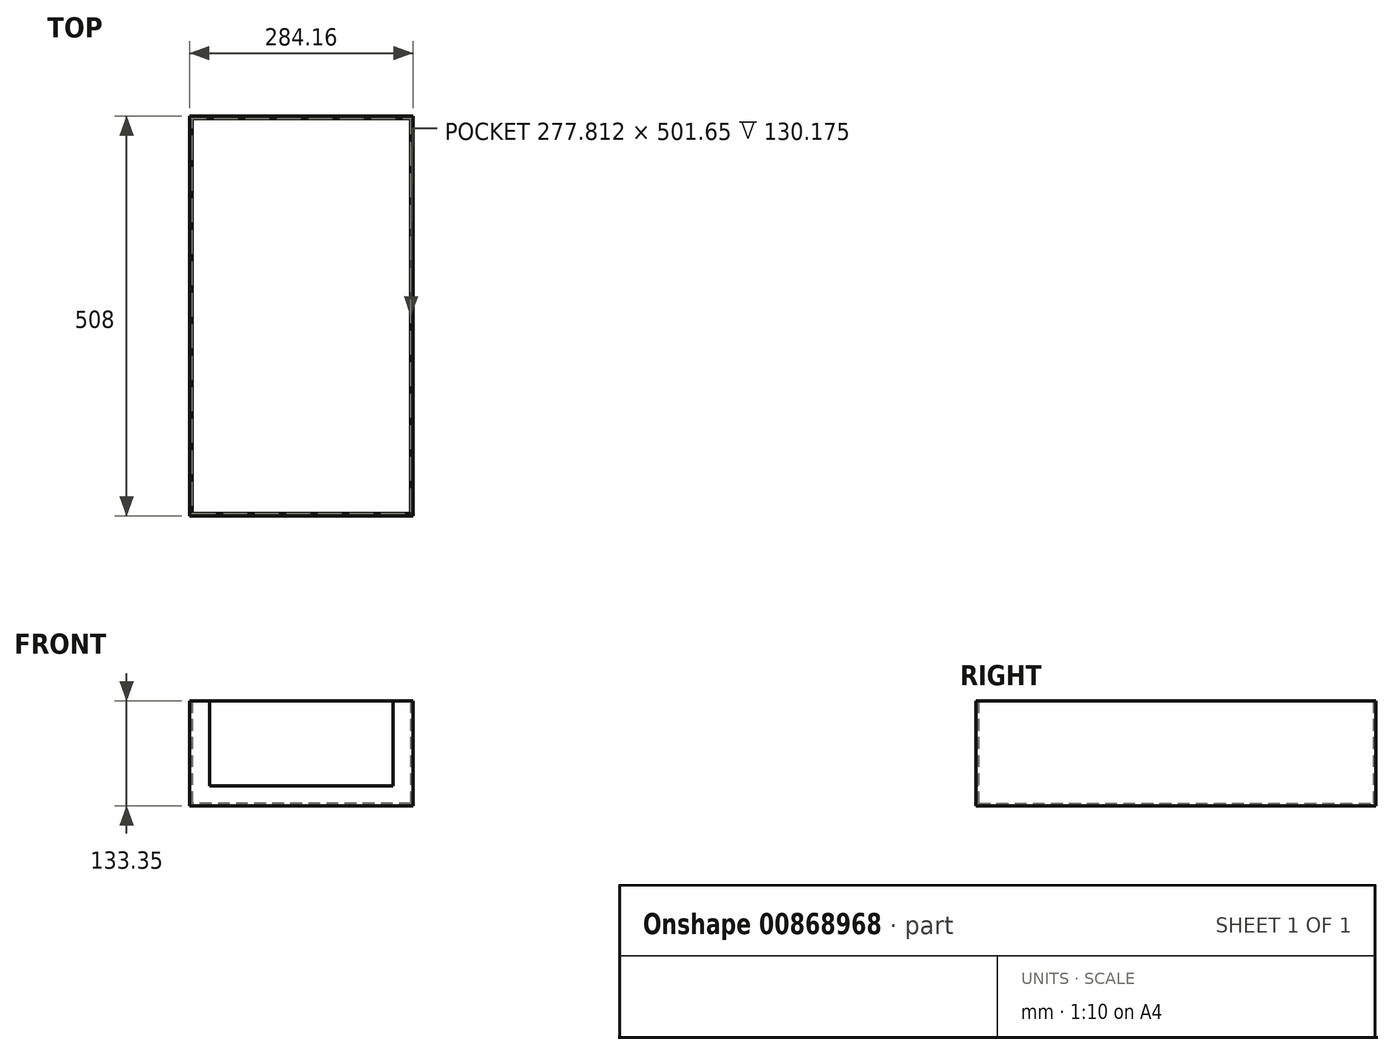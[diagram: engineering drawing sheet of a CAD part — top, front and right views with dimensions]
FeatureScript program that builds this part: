
annotation { "Feature Type Name" : "Feature", "Feature Type Description" : "" }
export const myFeature = defineFeature(function(context is Context, id is Id, definition is map)
    precondition{}
    {
        {
            var Q0;
            Q0=qCreatedBy(makeId("Top.planeOp"),FACE);
            var sketch = newSketch(context, id + "F0", { "sketchPlane" : qUnion([Q0])});
            skLineSegment(sketch, "E0.bottom", {"start": v(0, 0) * mm, "end": v(-284.16, 0) * mm});
            skLineSegment(sketch, "E0.top", {"start": v(0, 508) * mm, "end": v(-284.16, 508) * mm});
            skLineSegment(sketch, "E0.left", {"start": v(0, 0) * mm, "end": v(0, 508) * mm});
            skLineSegment(sketch, "E0.right", {"start": v(-284.16, 0) * mm, "end": v(-284.16, 508) * mm});
            skSolve(sketch);
        }
        {
            var Q0;
            Q0 = qSketchRegion(id + "F0", true);
            extrude(context, id + "F1", {"entities" : qUnion([Q0]), "depth" : 133.35 * mm, "offsetDistance" : 25.4 * mm});
        }
        {
            var Q0;
            Q0=makeQuery(id+"F1.opExtrude","CAP_FACE",FACE,{"disambiguationData":[OSD([sQuery(id+"F0.wireOp",EDGE,"E0.bottom"),sQuery(id+"F0.wireOp",EDGE,"E0.top"),sQuery(id+"F0.wireOp",EDGE,"E0.left"),sQuery(id+"F0.wireOp",EDGE,"E0.right")])],"isStart":false});
            shell(context, id + "F2", {"entities" : qUnion([Q0]), "thickness" : 3.17 * mm});
        }
        {
            var Q0;
            Q0=makeQuery(id+"F1.opExtrude","SWEPT_FACE",FACE,{"disambiguationData":[OSD([sQuery(id+"F0.wireOp",EDGE,"E0.bottom")])]});
            var sketch = newSketch(context, id + "F3", { "sketchPlane" : qUnion([Q0])});
            skLineSegment(sketch, "E1", {"start": v(-258.76, 133.35) * mm, "end": v(-258.76, 25.4) * mm});
            skLineSegment(sketch, "E2", {"start": v(-258.76, 25.4) * mm, "end": v(-25.4, 25.4) * mm});
            skLineSegment(sketch, "E3", {"start": v(-25.4, 25.4) * mm, "end": v(-25.4, 133.35) * mm});
            skLineSegment(sketch, "E4", {"start": v(-25.4, 133.35) * mm, "end": v(-258.76, 133.35) * mm});
            skSolve(sketch);
        }
        {
            var Q0;
            Q0 = qSketchRegion(id + "F3", true);
            extrude(context, id + "F4", {"entities" : qUnion([Q0]), "operationType" : NewBodyOperationType.REMOVE, "oppositeDirection" : true, "depth" : 25.4 * mm, "offsetDistance" : 25.4 * mm});
        }
    });
